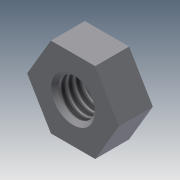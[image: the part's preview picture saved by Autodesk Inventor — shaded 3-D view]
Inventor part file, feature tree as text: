
AUTODESK INVENTOR PART (.ipt)
format: ipt  version: 2013 (Build 170138000, 138)  size: 90,112 bytes
history: native  units: mm
features: chamfer x2, sketch x2, extrude x1, hole x1
ambient origin geometry x8: Origin, YZ Plane, XZ Plane, XY Plane, X Axis, Y Axis, Z Axis, Center Point
bodies: Solid1 (feature_tree)
feature tree (6):
  extrude  "Extrusion1"  Depth=5.45mm
  hole  "Hole1"  [1 undecoded]
  chamfer  "Chamfer1"  Distance=0.25mm Angle=45.0deg
  chamfer  "Chamfer2"  [1 undecoded]
  sketch  "Sketch1"  dims[d5=3.0mm d6=5.45mm]
  sketch  "Sketch2"  dims[d7=2.3mm d8=0.0mm d9=2.459mm d10=6.0mm d11=4.0mm d12=2.0mm d13=90.0deg d14=8.0mm d15=0.0mm d16=0.25mm d17=2.0mm d18=45.0deg d19=0.25mm d20=2.0mm d21=45.0deg]
note: 2 required parameter values undecoded (feature->parameter linkage not recoverable at this tier; creation-order binding heuristic only, values carry confidence <= 0.55)
